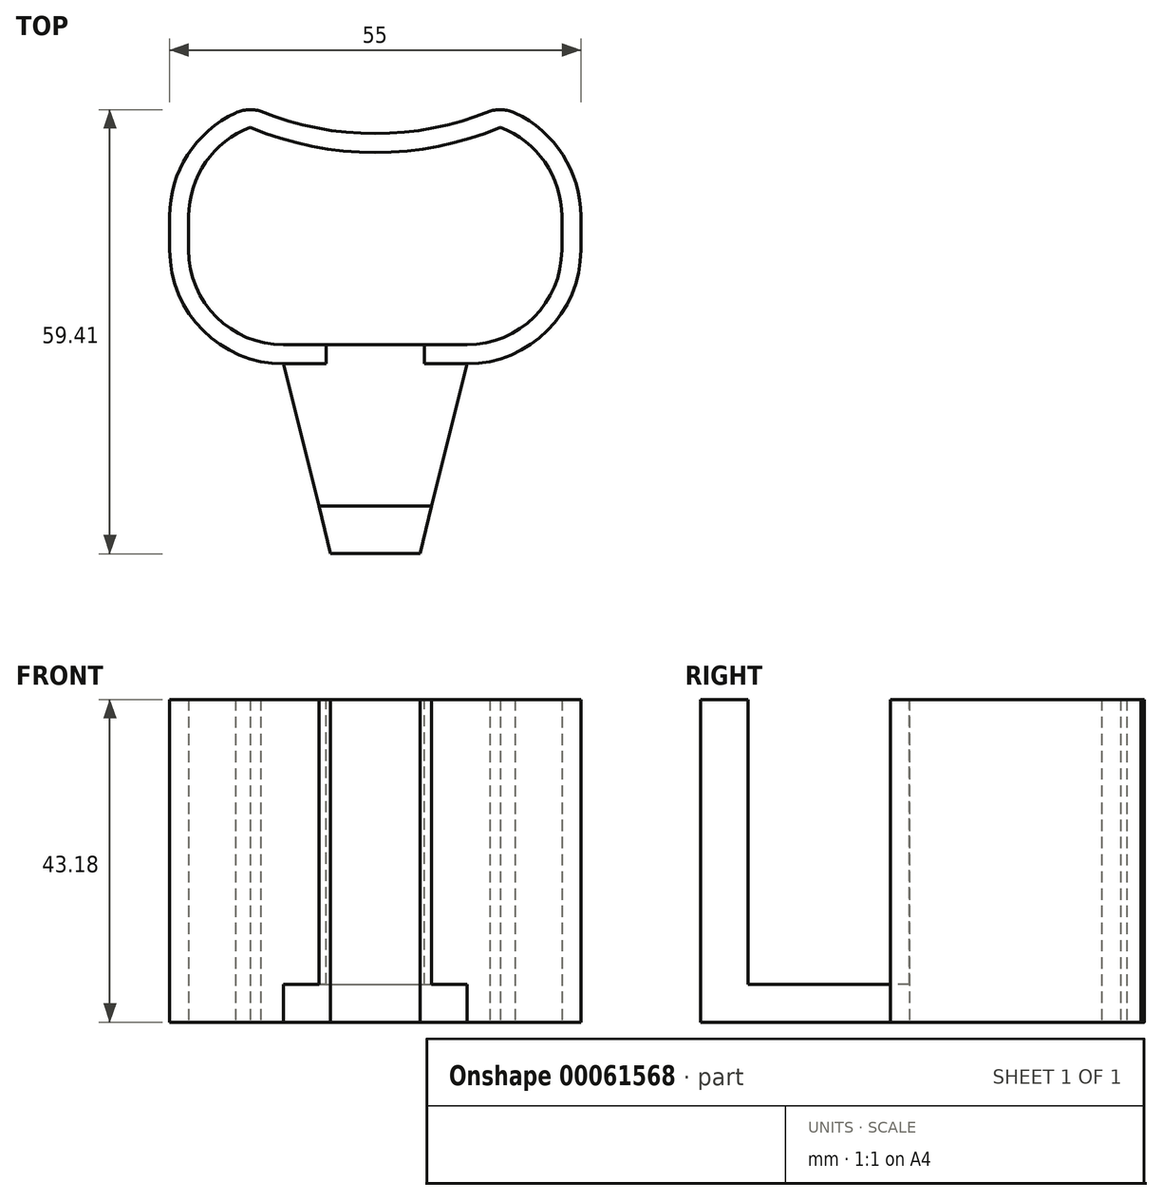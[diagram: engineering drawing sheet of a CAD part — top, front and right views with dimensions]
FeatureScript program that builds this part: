
annotation { "Feature Type Name" : "Feature", "Feature Type Description" : "" }
export const myFeature = defineFeature(function(context is Context, id is Id, definition is map)
    precondition{}
    {
        {
            var Q0;
            Q0=qCreatedBy(makeId("Top.planeOp"),FACE);
            var sketch = newSketch(context, id + "F0", { "sketchPlane" : qUnion([Q0])});
            skLineSegment(sketch, "E0.top", {"start": v(-20.48, -14.9) * mm, "end": v(-14.57, -14.9) * mm});
            skLineSegment(sketch, "E0.left", {"start": v(-35.72, 4.85) * mm, "end": v(-35.72, 0.33) * mm});
            skLineSegment(sketch, "E0.right", {"start": v(19.28, 4.85) * mm, "end": v(19.28, 0.33) * mm});
            skPoint(sketch, "E1.visualSharp", {"position": v(-35.72, 20.1) * mm});
            skArc(sketch, "E1.filletArc", {"start": v(-26.9, 18.68) * mm, "mid": v(-33.33, 13.05) * mm, "end": v(-35.72, 4.85) * mm});
            skPoint(sketch, "E2.visualSharp", {"position": v(-35.72, -14.9) * mm});
            skArc(sketch, "E2.filletArc", {"start": v(-35.72, 0.33) * mm, "mid": v(-31.26, -10.44) * mm, "end": v(-20.48, -14.9) * mm});
            skPoint(sketch, "E3.visualSharp", {"position": v(19.28, -14.9) * mm});
            skArc(sketch, "E3.filletArc", {"start": v(4.04, -14.9) * mm, "mid": v(14.81, -10.44) * mm, "end": v(19.28, 0.33) * mm});
            skPoint(sketch, "E4.visualSharp", {"position": v(19.28, 20.1) * mm});
            skArc(sketch, "E4.filletArc", {"start": v(19.28, 4.85) * mm, "mid": v(16.88, 13.05) * mm, "end": v(10.45, 18.68) * mm});
            skArc(sketch, "E5.0", {"start": v(-24.96, 16.74) * mm, "mid": v(-30.93, 12.08) * mm, "end": v(-33.18, 4.85) * mm});
            skLineSegment(sketch, "E5.1", {"start": v(-33.18, 4.85) * mm, "end": v(-33.18, 0.33) * mm});
            skArc(sketch, "E5.3", {"start": v(-33.18, 0.33) * mm, "mid": v(-29.46, -8.65) * mm, "end": v(-20.48, -12.37) * mm});
            skArc(sketch, "E5.4", {"start": v(16.74, 4.85) * mm, "mid": v(14.48, 12.08) * mm, "end": v(8.51, 16.74) * mm});
            skLineSegment(sketch, "E5.5", {"start": v(16.74, 4.85) * mm, "end": v(16.74, 0.33) * mm});
            skArc(sketch, "E5.6", {"start": v(4.04, -12.37) * mm, "mid": v(13.02, -8.65) * mm, "end": v(16.74, 0.33) * mm});
            skLineSegment(sketch, "E5.7", {"start": v(-20.48, -12.37) * mm, "end": v(-14.57, -12.37) * mm});
            skLineSegment(sketch, "E6", {"start": v(-8.22, 20.1) * mm, "end": v(-8.22, -40.3) * mm, "construction": true});
            skLineSegment(sketch, "E7.0", {"start": v(-14.57, -12.37) * mm, "end": v(-14.57, -14.9) * mm});
            skLineSegment(sketch, "E8.MirrorCS", {"start": v(-1.87, -12.37) * mm, "end": v(-1.87, -14.9) * mm});
            skPoint(sketch, "E9.orphan", {"position": v(-14.57, -24.22) * mm});
            skPoint(sketch, "E10.orphan", {"position": v(-1.87, -24.22) * mm});
            skLineSegment(sketch, "E11.trimOffspring", {"start": v(-1.87, -14.9) * mm, "end": v(4.04, -14.9) * mm});
            skLineSegment(sketch, "E12.trimOffspring", {"start": v(-1.87, -12.37) * mm, "end": v(4.04, -12.37) * mm});
            skPoint(sketch, "E13.orphan", {"position": v(-8.22, -12.37) * mm});
            skLineSegment(sketch, "E14", {"start": v(-8.22, 0) * mm, "end": v(-26.9, 18.68) * mm, "construction": true});
            skLineSegment(sketch, "E15.MirrorCS", {"start": v(-8.22, 0) * mm, "end": v(10.45, 18.68) * mm, "construction": true});
            skArc(sketch, "E16", {"start": v(-24.96, 16.74) * mm, "mid": v(-8.22, 13.37) * mm, "end": v(8.51, 16.74) * mm});
            skArc(sketch, "E17.0", {"start": v(-23.54, 18.9) * mm, "mid": v(-8.22, 15.9) * mm, "end": v(7.1, 18.9) * mm});
            skArc(sketch, "E18", {"start": v(-23.54, 18.9) * mm, "mid": v(-25.24, 19.1) * mm, "end": v(-26.9, 18.68) * mm});
            skArc(sketch, "E19.MirrorCS", {"start": v(7.1, 18.9) * mm, "mid": v(8.8, 19.1) * mm, "end": v(10.45, 18.68) * mm});
            skLineSegment(sketch, "E20", {"start": v(-20.48, -14.9) * mm, "end": v(-14.2, -40.3) * mm});
            skLineSegment(sketch, "E21", {"start": v(-14.57, -14.9) * mm, "end": v(-1.87, -14.9) * mm, "construction": true});
            skLineSegment(sketch, "E22.0", {"start": v(-14.2, -40.3) * mm, "end": v(-2.25, -40.3) * mm});
            skLineSegment(sketch, "E23.MirrorCS", {"start": v(4.04, -14.9) * mm, "end": v(-2.25, -40.3) * mm});
            skPoint(sketch, "E24.orphan", {"position": v(-4, -47.41) * mm});
            skPoint(sketch, "E25.orphan", {"position": v(-12.44, -47.41) * mm});
            skLineSegment(sketch, "E26", {"start": v(-14.57, -12.37) * mm, "end": v(-1.87, -12.37) * mm});
            skPoint(sketch, "E27.orphan", {"position": v(-32.86, 24.64) * mm});
            skPoint(sketch, "E28.orphan", {"position": v(16.41, 24.64) * mm});
            skSolve(sketch);
        }
        {
            var Q0;
            Q0=qSketchRegion(id+"F0",true);
            extrude(context, id + "F1", {"entities" : qUnion([Q0]), "depth" : 5.08 * mm});
        }
        {
            var Q0;
            Q0=makeQuery(id+"F1.opExtrude","CAP_FACE",FACE,{"disambiguationData":[OSD([sQuery(id+"F0.wireOp",EDGE,"E0.left"),sQuery(id+"F0.wireOp",EDGE,"E0.right"),sQuery(id+"F0.wireOp",EDGE,"E1.filletArc"),sQuery(id+"F0.wireOp",EDGE,"E2.filletArc"),sQuery(id+"F0.wireOp",EDGE,"E3.filletArc"),sQuery(id+"F0.wireOp",EDGE,"E4.filletArc"),sQuery(id+"F0.wireOp",EDGE,"E5.0"),sQuery(id+"F0.wireOp",EDGE,"E5.1"),sQuery(id+"F0.wireOp",EDGE,"E5.3"),sQuery(id+"F0.wireOp",EDGE,"E5.4"),sQuery(id+"F0.wireOp",EDGE,"E5.5"),sQuery(id+"F0.wireOp",EDGE,"E5.6"),sQuery(id+"F0.wireOp",EDGE,"E5.7"),sQuery(id+"F0.wireOp",EDGE,"E12.trimOffspring"),sQuery(id+"F0.wireOp",EDGE,"E16"),sQuery(id+"F0.wireOp",EDGE,"E17.0"),sQuery(id+"F0.wireOp",EDGE,"E18"),sQuery(id+"F0.wireOp",EDGE,"E19.MirrorCS"),sQuery(id+"F0.wireOp",EDGE,"E20"),sQuery(id+"F0.wireOp",EDGE,"E22.0"),sQuery(id+"F0.wireOp",EDGE,"E23.MirrorCS"),sQuery(id+"F0.wireOp",EDGE,"E26")])],"isStart":false});
            extrude(context, id + "F2", {"entities" : qUnion([Q0]), "operationType" : NewBodyOperationType.ADD, "depth" : 38.1 * mm});
        }
        {
            var Q0;
            Q0=makeQuery(id+"F2.opExtrude","CAP_FACE",FACE,{"disambiguationData":[OSD([sQuery(id+"F0.wireOp",EDGE,"E0.left"),sQuery(id+"F0.wireOp",EDGE,"E0.right"),sQuery(id+"F0.wireOp",EDGE,"E1.filletArc"),sQuery(id+"F0.wireOp",EDGE,"E2.filletArc"),sQuery(id+"F0.wireOp",EDGE,"E3.filletArc"),sQuery(id+"F0.wireOp",EDGE,"E4.filletArc"),sQuery(id+"F0.wireOp",EDGE,"E5.0"),sQuery(id+"F0.wireOp",EDGE,"E5.1"),sQuery(id+"F0.wireOp",EDGE,"E5.3"),sQuery(id+"F0.wireOp",EDGE,"E5.4"),sQuery(id+"F0.wireOp",EDGE,"E5.5"),sQuery(id+"F0.wireOp",EDGE,"E5.6"),sQuery(id+"F0.wireOp",EDGE,"E5.7"),sQuery(id+"F0.wireOp",EDGE,"E12.trimOffspring"),sQuery(id+"F0.wireOp",EDGE,"E16"),sQuery(id+"F0.wireOp",EDGE,"E17.0"),sQuery(id+"F0.wireOp",EDGE,"E18"),sQuery(id+"F0.wireOp",EDGE,"E19.MirrorCS"),sQuery(id+"F0.wireOp",EDGE,"E20"),sQuery(id+"F0.wireOp",EDGE,"E22.0"),sQuery(id+"F0.wireOp",EDGE,"E23.MirrorCS"),sQuery(id+"F0.wireOp",EDGE,"E26")])],"isStart":false});
            var sketch = newSketch(context, id + "F3", { "sketchPlane" : qUnion([Q0])});
            skLineSegment(sketch, "E29", {"start": v(-8.22, -12.37) * mm, "end": v(-8.22, -33.96) * mm});
            skLineSegment(sketch, "E30", {"start": v(-14.2, -40.3) * mm, "end": v(-2.25, -40.3) * mm});
            skLineSegment(sketch, "E31.0", {"start": v(-16.58, -33.96) * mm, "end": v(-2.25, -33.96) * mm});
            skLineSegment(sketch, "E32", {"start": v(-8.22, -12.37) * mm, "end": v(-14.77, -12.37) * mm});
            skLineSegment(sketch, "E33", {"start": v(-14.77, -12.37) * mm, "end": v(-14.77, -14.9) * mm});
            skLineSegment(sketch, "E34", {"start": v(-14.77, -14.9) * mm, "end": v(-26.79, -14.9) * mm});
            skLineSegment(sketch, "E35", {"start": v(-26.79, -14.9) * mm, "end": v(-16.58, -33.96) * mm});
            skLineSegment(sketch, "E36.MirrorCS", {"start": v(-8.22, -12.37) * mm, "end": v(-1.68, -12.37) * mm});
            skLineSegment(sketch, "E37.MirrorCS", {"start": v(-1.68, -12.37) * mm, "end": v(-1.68, -14.9) * mm});
            skLineSegment(sketch, "E38.MirrorCS", {"start": v(-1.68, -14.9) * mm, "end": v(10.34, -14.9) * mm});
            skLineSegment(sketch, "E39.MirrorCS", {"start": v(10.34, -14.9) * mm, "end": v(0.13, -33.96) * mm});
            skLineSegment(sketch, "E40.MirrorCS", {"start": v(0.13, -33.96) * mm, "end": v(-14.2, -33.96) * mm});
            skSolve(sketch);
        }
        {
            var Q0;
            Q0 = qSketchRegion(id + "F3", true);
            extrude(context, id + "F4", {"entities" : qUnion([Q0]), "operationType" : NewBodyOperationType.REMOVE, "oppositeDirection" : true, "depth" : 38.1 * mm});
        }
    });
